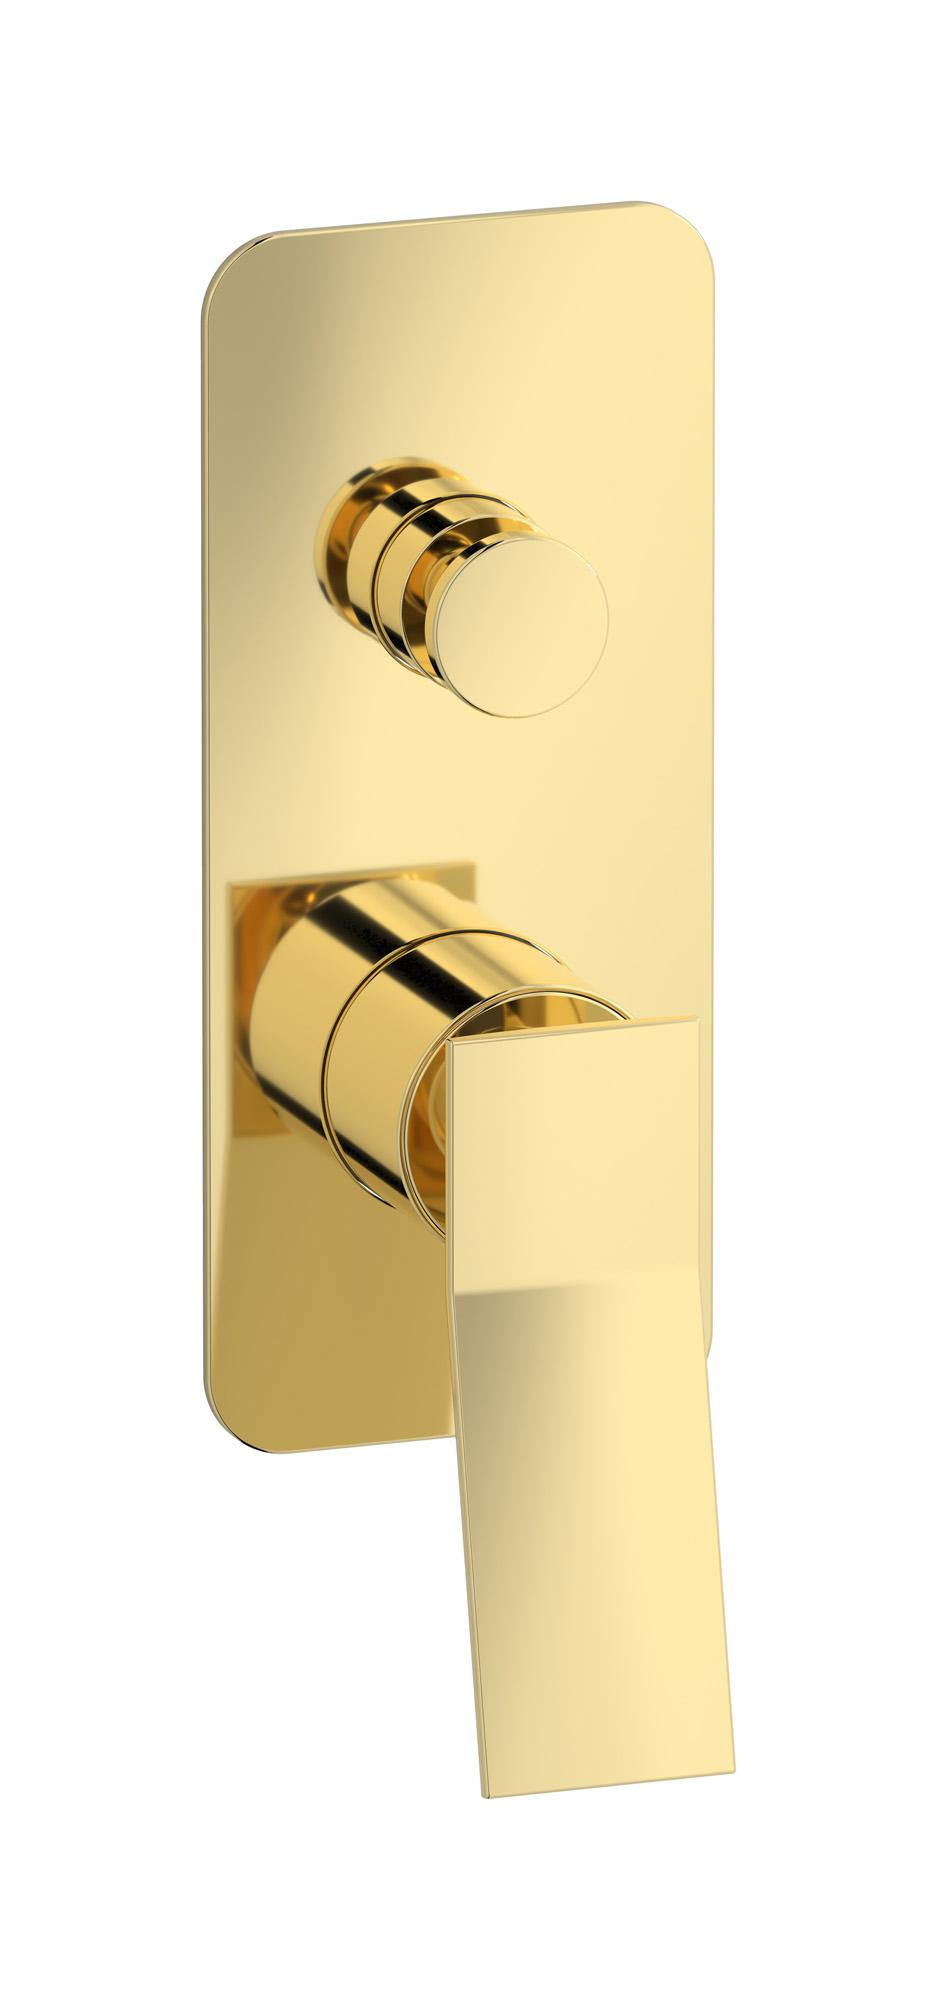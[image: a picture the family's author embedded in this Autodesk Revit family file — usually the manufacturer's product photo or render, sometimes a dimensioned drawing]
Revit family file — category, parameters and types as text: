
# Revit family: WA310
name_source: partatom
category: Apparecchi idraulici
units: mm (PartAtom-declared; Revit-internal decimal feet)

## family parameters
Basato su piano di lavoro = No
Condiviso = No
Mantieni orientamento annotazione = No
Numero OmniClass = 23.45.55.17
Punto di calcolo locali = No
Quota connettore circolare = Usa diametro
Sempre verticale = Sì
Taglio con vuoti quando caricato = No
Tipo di parte = Normale
Titolo OmniClass = Mixing Faucets

## types (12) — shared parameters
Cold water inlet = 10 mm  [stored 0.0328084 ft]
Commenti sul tipo = Wall mixer
Connessione CW = No
Connessione HW = No
Connessione di scarico = No
Connessione di ventilazione = No
Descrizione = Exposed parts for manual wall mixer with two ways diverter
Hot water inlet = 10 mm  [stored 0.0328084 ft]
Produttore = IB Rubinetterie S.p.A.
URL = https://www.weareib.it
zero-valued in all types: Prospetto di default

## per-type parameters (varying)
| type | Finishes surface | Immagine tipo | Modello |
| Chrome | IB_Chrome | WA310CC.jpg | WA310CC |
| Brushed nickel | IB_Brushed nickel | WA310SS.jpg | WA310SS |
| Matt black | IB_matt black | WA310NP.jpg | WA310NP |
| Matt white | IB_matt white | WA310BO.jpg | WA310BO |
| Black chrome | IB_Black chrome | WA310CF.jpg | WA310CF |
| Brushed black chrome | IB_Brushed black chrome | WA310CS.jpg | WA310CS |
| Pale gold | IB_Pale gold | WA310II.jpg | WA310II |
| Brushed pale gold | IB_brushed pale gold | WA310IS.jpg | WA310IS |
| Rose gold | IB_Rose gold | WA310RS.jpg | WA310RS |
| Brushed rose gold | IB_Brushed rose gold | WA310SR.jpg | WA310SR |
| Gold | IB_gold | WA310OO.jpg | WA310OO |
| Brushed gold | IB_brushed gold | WA310OS.jpg | WA310OS |

note: [stored X ft] marks values corroborated as IEEE doubles in the binary element streams (Revit-internal decimal feet)
